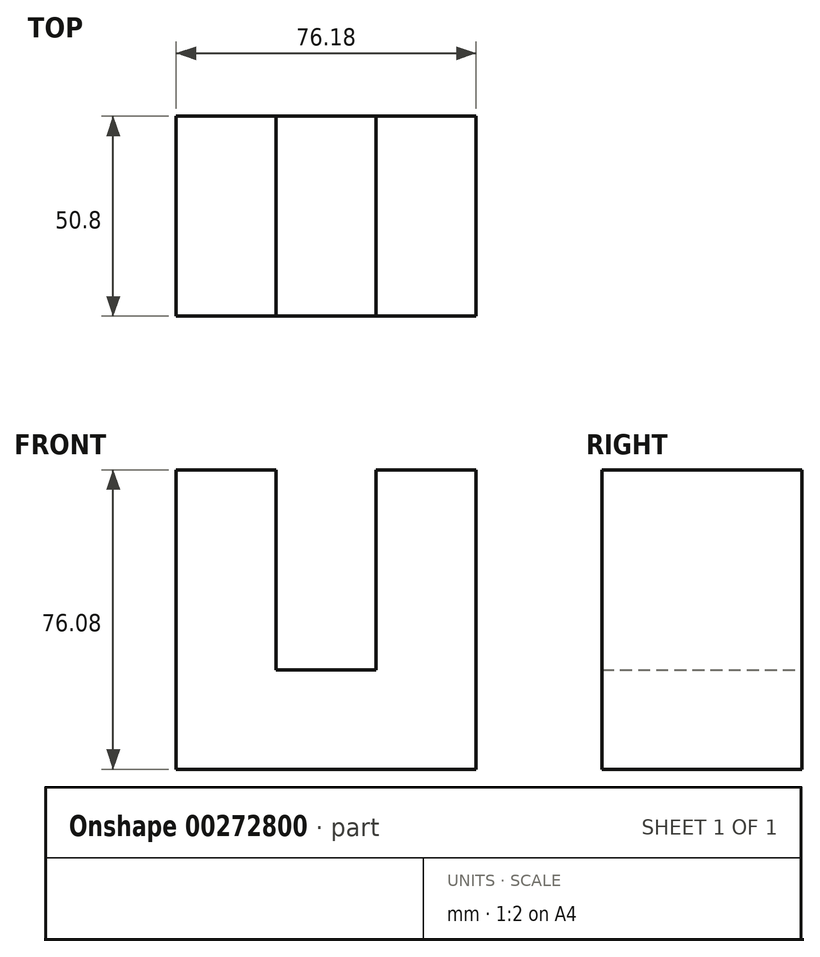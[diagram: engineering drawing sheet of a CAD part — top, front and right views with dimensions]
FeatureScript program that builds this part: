
annotation { "Feature Type Name" : "Feature", "Feature Type Description" : "" }
export const myFeature = defineFeature(function(context is Context, id is Id, definition is map)
    precondition{}
    {
        {
            var Q0;
            Q0=qCreatedBy(makeId("Front.planeOp"),FACE);
            var sketch = newSketch(context, id + "F0", { "sketchPlane" : qUnion([Q0])});
            skLineSegment(sketch, "E0", {"start": v(-76.18, 76.08) * mm, "end": v(-76.18, 0) * mm});
            skLineSegment(sketch, "E1", {"start": v(-76.18, 0) * mm, "end": v(0, 0) * mm});
            skLineSegment(sketch, "E2", {"start": v(0, 76.08) * mm, "end": v(0, 0) * mm});
            skLineSegment(sketch, "E3", {"start": v(0, 76.08) * mm, "end": v(-25.4, 76.08) * mm});
            skLineSegment(sketch, "E4", {"start": v(-76.18, 76.08) * mm, "end": v(-50.78, 76.08) * mm});
            skLineSegment(sketch, "E5", {"start": v(-50.78, 76.08) * mm, "end": v(-50.78, 25.28) * mm});
            skLineSegment(sketch, "E6", {"start": v(-25.4, 76.08) * mm, "end": v(-25.4, 25.28) * mm});
            skLineSegment(sketch, "E7", {"start": v(-50.78, 25.28) * mm, "end": v(-25.4, 25.28) * mm});
            skSolve(sketch);
        }
        {
            var Q0;
            Q0 = qSketchRegion(id + "F0", true);
            extrude(context, id + "F1", {"entities" : qUnion([Q0]), "depth" : 50.8 * mm});
        }
    });
